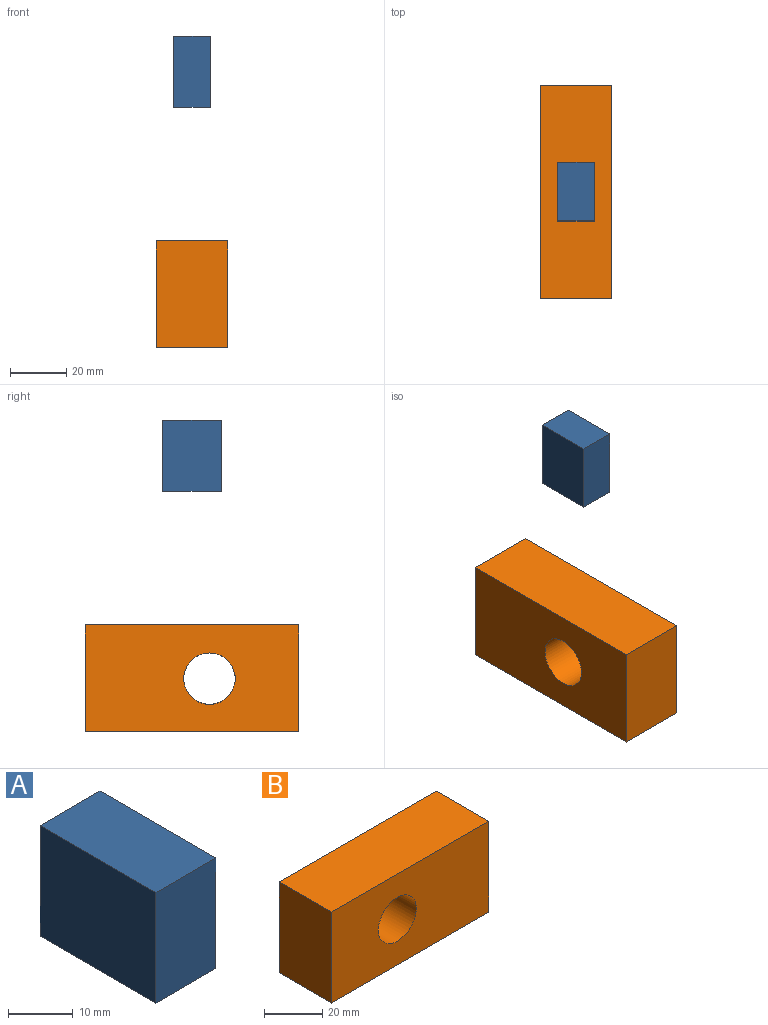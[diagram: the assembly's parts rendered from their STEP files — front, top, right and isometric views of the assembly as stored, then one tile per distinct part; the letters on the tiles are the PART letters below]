
ASSEMBLY  parts=2 mates=1
PART A: 6 faces, bbox 13.1x25.4x20.9 mm
  f0: plane 25.4x20.95mm, normal (-1,0,0), area 532.1mm2, adj f1,f3,f4,f5
  f1: plane 25.4x13.14mm, normal (0,0,-1), area 333.7mm2, adj f0,f2,f4,f5
  f2: plane 25.4x20.95mm, normal (1,0,0), area 532.1mm2, adj f1,f3,f4,f5
  f3: plane 25.4x13.14mm, normal (0,0,1), area 333.7mm2, adj f0,f2,f4,f5
  f4: plane 20.95x13.14mm, normal (0,-1,0), area 275.2mm2, adj f0,f1,f2,f3
  f5: plane 20.95x13.14mm, normal (0,1,0), area 275.2mm2, adj f0,f1,f2,f3
PART B: 7 faces, bbox 76.2x25.4x38.1 mm
  f0: plane 76.2x25.4mm, normal (0,0,1), area 1935.5mm2, adj f1,f3,f4,f5
  f1: plane 38.1x25.4mm, normal (-1,0,0), area 967.7mm2, adj f0,f2,f4,f5
  f2: plane 76.2x25.4mm, normal (0,0,-1), area 1935.5mm2, adj f1,f3,f4,f5
  f3: plane 38.1x25.4mm, normal (1,0,0), area 967.7mm2, adj f0,f2,f4,f5
  f4: plane 76.2x38.1mm, normal (0,-1,0), area 2639.1mm2, adj f0,f1,f2,f3,f6
  f5: plane 76.2x38.1mm, normal (0,1,0), area 2639.1mm2, adj f0,f1,f2,f3,f6
  f6: cylinder r=9.17mm len=25.4mm, axis (0,1,0), area 1463.2mm2, adj f4,f5
PLACE A rot(axis=(1,0,0),90deg) t=(36.72,-27.63,111.11)mm
PLACE B rot(axis=(0.71,0.71,0),180deg) t=(25.4,-76.2,0)mm fixed
MATE slider A.f4 <-> B.f2  axis (0,0,-1) through (12.7,-38.1,85.71)mm
